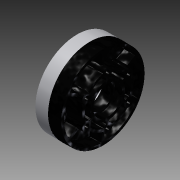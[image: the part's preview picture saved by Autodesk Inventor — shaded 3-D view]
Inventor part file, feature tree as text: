
AUTODESK INVENTOR PART (.ipt)
format: ipt  version: 2015 (Build 190159000, 159)  size: 1,608,704 bytes
history: native  units: in
note: dims shown in document units (in); Inventor stores cm internally (conversion verified against a paired STEP export)
features: fillet x2, imported_body x2, other x1
ambient origin geometry x8: Origin, YZ Plane, XZ Plane, XY Plane, X Axis, Y Axis, Z Axis, Center Point
bodies: Body1 (feature_tree), Body2 (feature_tree)
feature tree (5):
  fillet  "Fillet10"  [1 undecoded]
  other  "4in 2013 Hub.ipt1"
  fillet  "Fillet9"  [1 undecoded]
  imported_body  "Base1"
  imported_body  "Base2"
note: 2 required parameter values undecoded (feature->parameter linkage not recoverable at this tier; creation-order binding heuristic only, values carry confidence <= 0.55)
